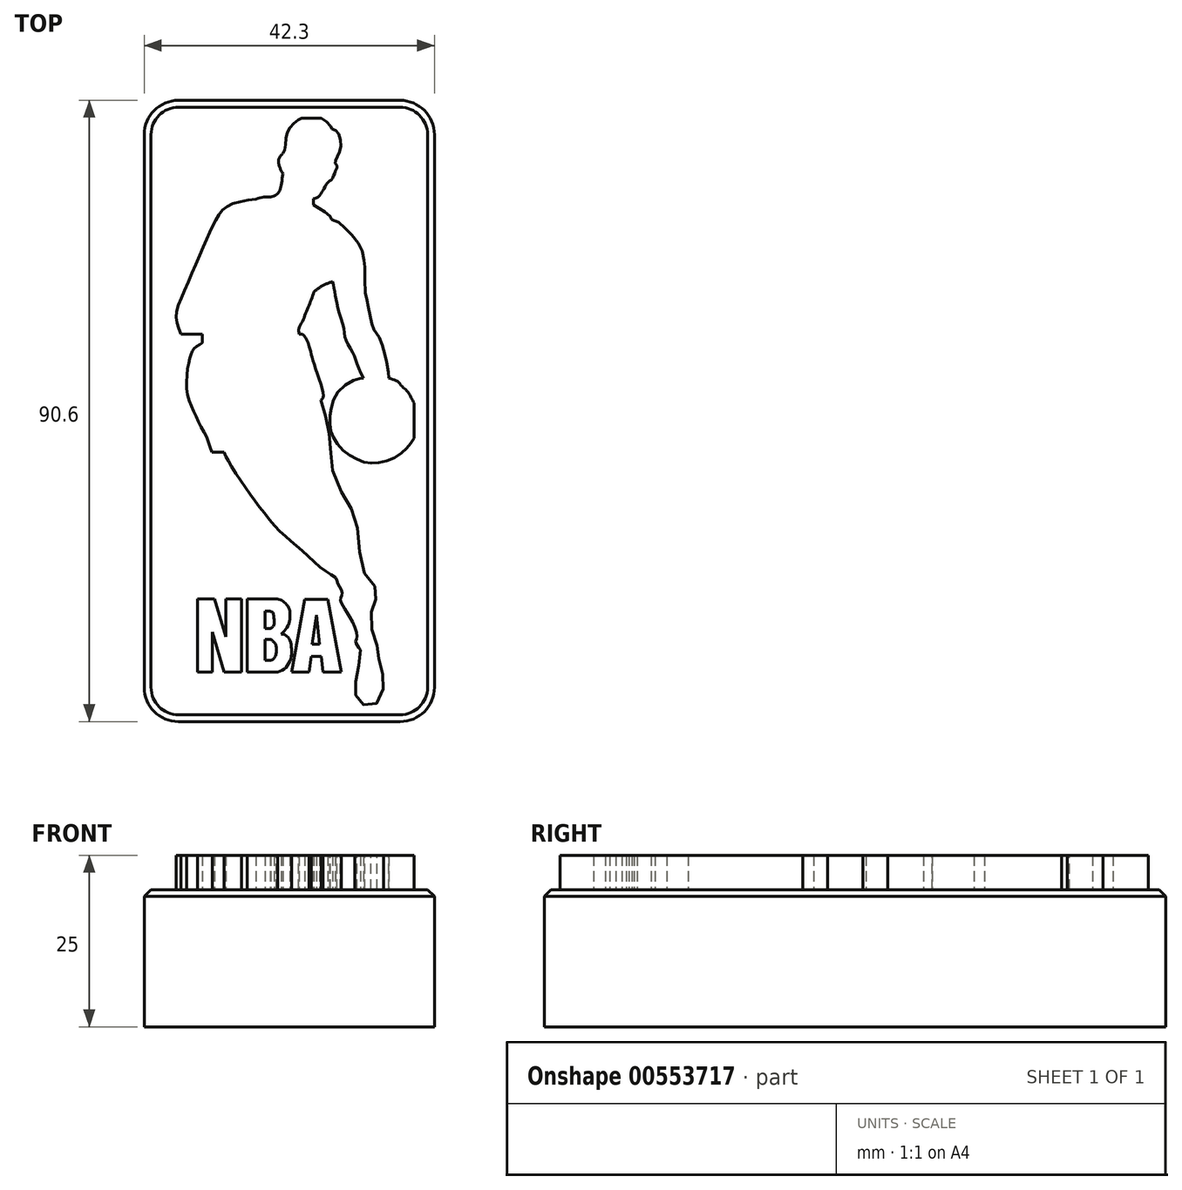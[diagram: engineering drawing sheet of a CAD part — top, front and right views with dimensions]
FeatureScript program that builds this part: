
annotation { "Feature Type Name" : "Feature", "Feature Type Description" : "" }
export const myFeature = defineFeature(function(context is Context, id is Id, definition is map)
    precondition{}
    {
        {
            var Q0;
            Q0=qCreatedBy(makeId("Top.planeOp"),FACE);
            var sketch = newSketch(context, id + "F0", { "sketchPlane" : qUnion([Q0])});
            skLineSegment(sketch, "E0", {"start": v(49.46, 96.34) * mm, "end": v(49.46, 0) * mm, "construction": true});
            skLineSegment(sketch, "E1", {"start": v(0, 48.17) * mm, "end": v(98.91, 48.17) * mm, "construction": true});
            skLineSegment(sketch, "E2.bottom", {"start": v(70.6, 93.47) * mm, "end": v(28.3, 93.47) * mm});
            skLineSegment(sketch, "E2.top", {"start": v(70.6, 2.87) * mm, "end": v(28.3, 2.87) * mm});
            skLineSegment(sketch, "E2.left", {"start": v(70.6, 93.47) * mm, "end": v(70.6, 2.87) * mm});
            skLineSegment(sketch, "E2.right", {"start": v(28.3, 93.47) * mm, "end": v(28.3, 2.87) * mm});
            skPoint(sketch, "E2.middle", {"position": v(49.46, 48.17) * mm});
            skSolve(sketch);
        }
        {
            var Q0;
            Q0 = qSketchRegion(id + "F0", true);
            extrude(context, id + "F1", {"entities" : qUnion([Q0]), "depth" : 20 * mm, "offsetDistance" : 25 * mm});
        }
        {
            var Q0;
            Q0=qCreatedBy(makeId("Top.planeOp"),FACE);
            var sketch = newSketch(context, id + "F2", { "sketchPlane" : qUnion([Q0])});
            skLineSegment(sketch, "E3", {"start": v(36.08, 10.07) * mm, "end": v(36.06, 20.74) * mm});
            skLineSegment(sketch, "E4", {"start": v(36.06, 20.74) * mm, "end": v(38.53, 20.74) * mm});
            skLineSegment(sketch, "E5", {"start": v(38.53, 20.74) * mm, "end": v(40.2, 15.23) * mm});
            skLineSegment(sketch, "E6", {"start": v(40.2, 15.23) * mm, "end": v(40.2, 20.74) * mm});
            skLineSegment(sketch, "E7", {"start": v(40.2, 20.74) * mm, "end": v(42.53, 20.74) * mm});
            skLineSegment(sketch, "E8", {"start": v(42.53, 20.74) * mm, "end": v(42.53, 10.07) * mm});
            skLineSegment(sketch, "E9", {"start": v(42.53, 10.07) * mm, "end": v(39.96, 10.07) * mm});
            skLineSegment(sketch, "E10", {"start": v(39.96, 10.07) * mm, "end": v(38.25, 15.94) * mm});
            skLineSegment(sketch, "E11", {"start": v(38.25, 15.94) * mm, "end": v(38.25, 10.07) * mm});
            skLineSegment(sketch, "E12", {"start": v(38.25, 10.07) * mm, "end": v(36.08, 10.07) * mm});
            skLineSegment(sketch, "E13", {"start": v(43.32, 10.07) * mm, "end": v(43.3, 20.74) * mm});
            skLineSegment(sketch, "E14", {"start": v(43.3, 20.74) * mm, "end": v(47.68, 20.74) * mm});
            skLineSegment(sketch, "E15", {"start": v(43.32, 10.07) * mm, "end": v(47.75, 10.08) * mm});
            skFitSpline(sketch, "E16", {"points": [v(47.75, 10.08) * mm, v(48.77, 10.58) * mm, v(49.49, 11.58) * mm, v(49.77, 12.75) * mm, v(49.75, 13.92) * mm, v(49.51, 14.83) * mm, v(49.15, 15.29) * mm, v(48.83, 15.52) * mm, v(48.28, 15.65) * mm], "startDerivative": vector(7.59, 2.72) * mm, "endDerivative": vector(-5.94, 1) * mm});
            skFitSpline(sketch, "E17", {"points": [v(48.28, 15.65) * mm, v(48.94, 16.33) * mm, v(49.47, 17.44) * mm, v(49.53, 18.32) * mm, v(49.49, 19.2) * mm, v(49.21, 19.77) * mm, v(48.72, 20.3) * mm, v(48.28, 20.6) * mm, v(47.68, 20.74) * mm], "startDerivative": vector(4.95, 4.43) * mm, "endDerivative": vector(-5.76, 0.93) * mm});
            skLineSegment(sketch, "E18", {"start": v(45.94, 19) * mm, "end": v(45.94, 16.5) * mm});
            skFitSpline(sketch, "E19", {"points": [v(45.94, 19) * mm, v(46.53, 19) * mm, v(47, 18.82) * mm, v(47.2, 18.33) * mm, v(47.25, 17.67) * mm, v(47.25, 17.06) * mm, v(46.99, 16.64) * mm, v(46.7, 16.44) * mm], "startDerivative": vector(3.88, 0.21) * mm, "endDerivative": vector(-2.46, -1.47) * mm});
            skLineSegment(sketch, "E20", {"start": v(46.7, 16.44) * mm, "end": v(45.94, 16.44) * mm});
            skLineSegment(sketch, "E21", {"start": v(45.94, 16.44) * mm, "end": v(45.94, 16.5) * mm});
            skLineSegment(sketch, "E22", {"start": v(45.94, 14.83) * mm, "end": v(45.94, 11.81) * mm});
            skLineSegment(sketch, "E23", {"start": v(45.94, 11.81) * mm, "end": v(46.79, 11.81) * mm});
            skFitSpline(sketch, "E24", {"points": [v(46.79, 11.81) * mm, v(47.22, 12.07) * mm, v(47.53, 12.8) * mm, v(47.56, 13.65) * mm, v(47.4, 14.25) * mm, v(47, 14.66) * mm, v(46.79, 14.84) * mm], "startDerivative": vector(3, 1.25) * mm, "endDerivative": vector(-1.62, 1.47) * mm});
            skLineSegment(sketch, "E25", {"start": v(45.94, 14.83) * mm, "end": v(46.79, 14.84) * mm});
            skLineSegment(sketch, "E26", {"start": v(49.8, 10.08) * mm, "end": v(50.27, 10.08) * mm});
            skLineSegment(sketch, "E27", {"start": v(50.27, 10.08) * mm, "end": v(52.35, 10.09) * mm});
            skLineSegment(sketch, "E28", {"start": v(52.35, 10.09) * mm, "end": v(52.64, 12.4) * mm});
            skLineSegment(sketch, "E29", {"start": v(52.64, 12.4) * mm, "end": v(54.13, 12.4) * mm});
            skLineSegment(sketch, "E30", {"start": v(54.13, 12.4) * mm, "end": v(54.35, 10.08) * mm});
            skLineSegment(sketch, "E31", {"start": v(54.35, 10.08) * mm, "end": v(57.02, 10.1) * mm});
            skLineSegment(sketch, "E32", {"start": v(57.02, 10.1) * mm, "end": v(55.07, 20.7) * mm});
            skLineSegment(sketch, "E33", {"start": v(55.07, 20.7) * mm, "end": v(51.71, 20.7) * mm});
            skLineSegment(sketch, "E34", {"start": v(51.71, 20.7) * mm, "end": v(49.8, 10.08) * mm});
            skLineSegment(sketch, "E35", {"start": v(52.8, 14.19) * mm, "end": v(53.85, 14.19) * mm});
            skLineSegment(sketch, "E36", {"start": v(53.85, 14.19) * mm, "end": v(53.45, 18.42) * mm});
            skLineSegment(sketch, "E37", {"start": v(53.45, 18.42) * mm, "end": v(52.8, 14.19) * mm});
            skSolve(sketch);
        }
        {
            var Q0;
            Q0 = qSketchRegion(id + "F2", true);
            extrude(context, id + "F3", {"entities" : qUnion([Q0]), "operationType" : NewBodyOperationType.ADD, "depth" : 25 * mm, "offsetDistance" : 25 * mm});
        }
        {
            var Q0;
            Q0=qCreatedBy(makeId("Top.planeOp"),FACE);
            var sketch = newSketch(context, id + "F4", { "sketchPlane" : qUnion([Q0])});
            skFitSpline(sketch, "E38", {"points": [v(56.13, 84.27) * mm, v(56.38, 84.06) * mm, v(56.32, 83.43) * mm, v(56.07, 82.86) * mm, v(55.63, 81.93) * mm, v(55.23, 81.64) * mm, v(55.06, 81.53) * mm, v(54.6, 80.79) * mm, v(54.22, 80.1) * mm, v(53.88, 79.58) * mm, v(53.44, 79.24) * mm, v(52.94, 79.1) * mm], "startDerivative": vector(4.5, -2.2) * mm, "endDerivative": vector(-5.95, -1.06) * mm});
            skFitSpline(sketch, "E39", {"points": [v(52.94, 79.1) * mm, v(52.94, 78.25) * mm], "startDerivative": vector(0, -0.86) * mm, "endDerivative": vector(0, -0.86) * mm});
            skFitSpline(sketch, "E40", {"points": [v(52.94, 78.25) * mm, v(55.23, 76.82) * mm, v(55.42, 76.5) * mm, v(55.44, 76.18) * mm, v(56.1, 75.95) * mm, v(57.05, 75.4) * mm, v(58.11, 74.32) * mm, v(59.44, 72.75) * mm, v(60.08, 71.4) * mm, v(60.4, 69.88) * mm, v(60.48, 68.98) * mm, v(60.5, 65.62) * mm, v(60.72, 64.46) * mm, v(60.95, 63.55) * mm, v(61.19, 62.38) * mm, v(61.46, 61.03) * mm, v(61.64, 60.25) * mm, v(62.44, 59.13) * mm, v(63.02, 57.81) * mm, v(63.42, 56.2) * mm, v(63.72, 55.04) * mm, v(63.95, 53.3) * mm, v(63.93, 52.94) * mm], "startDerivative": vector(43.04, -24.8) * mm, "endDerivative": vector(-1.36, -11.13) * mm});
            skFitSpline(sketch, "E41", {"points": [v(63.93, 52.94) * mm, v(65.3, 52.44) * mm, v(65.82, 51.82) * mm, v(66.57, 51.15) * mm, v(67.18, 50.18) * mm, v(67.65, 49.33) * mm], "startDerivative": vector(6.8, -1.68) * mm, "endDerivative": vector(2.4, -4.31) * mm});
            skFitSpline(sketch, "E42", {"points": [v(67.65, 49.33) * mm, v(67.65, 44.18) * mm], "startDerivative": vector(0, -5.16) * mm, "endDerivative": vector(0, -5.16) * mm});
            skFitSpline(sketch, "E43", {"points": [v(67.65, 44.18) * mm, v(66.97, 43.24) * mm, v(66.13, 42.32) * mm, v(64.47, 41.17) * mm, v(62.47, 40.6) * mm, v(60.8, 40.62) * mm, v(59.17, 41.23) * mm, v(57.4, 42.34) * mm, v(56.09, 43.95) * mm, v(55.52, 45.24) * mm, v(55.39, 47.05) * mm, v(55.66, 48.91) * mm, v(56.6, 51.04) * mm, v(58.92, 52.66) * mm, v(59.94, 52.94) * mm, v(60.26, 52.94) * mm], "startDerivative": vector(-11.97, -17.16) * mm, "endDerivative": vector(9.83, -0.58) * mm});
            skFitSpline(sketch, "E44", {"points": [v(60.26, 52.94) * mm, v(59.23, 55.35) * mm, v(58.66, 56.77) * mm, v(57.7, 58.56) * mm, v(57.43, 59.99) * mm, v(56.7, 62.7) * mm, v(56.23, 64.65) * mm, v(55.98, 66) * mm, v(55.78, 67.05) * mm], "startDerivative": vector(-7.83, 17.22) * mm, "endDerivative": vector(-2.09, 10.68) * mm});
            skFitSpline(sketch, "E45", {"points": [v(55.78, 67.05) * mm, v(54.3, 66.44) * mm, v(53.03, 65.52) * mm], "startDerivative": vector(-3.05, -1.05) * mm, "endDerivative": vector(-2.45, -2) * mm});
            skFitSpline(sketch, "E46", {"points": [v(53.03, 65.52) * mm, v(52.58, 64.2) * mm, v(51.95, 62.72) * mm, v(51.36, 61.21) * mm, v(50.82, 60.12) * mm, v(50.91, 59.4) * mm], "startDerivative": vector(-1.92, -6.3) * mm, "endDerivative": vector(1.44, -4.65) * mm});
            skFitSpline(sketch, "E47", {"points": [v(50.91, 59.4) * mm, v(51.55, 59.24) * mm, v(52.44, 57.38) * mm, v(53.03, 55.16) * mm, v(54.43, 50.33) * mm, v(54.05, 49.77) * mm], "startDerivative": vector(5.44, 0.14) * mm, "endDerivative": vector(-4.4, -2.9) * mm});
            skFitSpline(sketch, "E48", {"points": [v(54.05, 49.77) * mm, v(54.73, 47.48) * mm, v(55.23, 45.12) * mm, v(55.52, 41.97) * mm, v(55.78, 39.46) * mm, v(57.5, 35.56) * mm, v(58.9, 33.04) * mm, v(59.62, 29) * mm, v(60.26, 24.8) * mm, v(61.78, 22.84) * mm, v(62.25, 21.32) * mm, v(61.75, 19.99) * mm, v(61.41, 18.58) * mm, v(61.55, 15.9) * mm, v(62.25, 13.82) * mm, v(62.39, 12.62) * mm, v(62.93, 10.42) * mm, v(63.18, 8.86) * mm, v(62.96, 6.61) * mm, v(61.78, 5.28) * mm, v(60.26, 5.35) * mm, v(59.38, 6.27) * mm, v(59.04, 7.27) * mm, v(59.24, 9.2) * mm, v(59.62, 11.3) * mm, v(59.8, 13.32) * mm], "startDerivative": vector(17.19, -55.33) * mm, "endDerivative": vector(3.4, 52.46) * mm});
            skFitSpline(sketch, "E49", {"points": [v(59.8, 13.32) * mm, v(59.38, 13.98) * mm, v(59.13, 14.61) * mm, v(59.35, 15.3) * mm, v(58.15, 18.35) * mm, v(57.15, 19.96) * mm, v(56.93, 20.92) * mm, v(57.18, 21.57) * mm, v(56.68, 22.77) * mm, v(56.25, 23.86) * mm], "startDerivative": vector(-4.75, 7.09) * mm, "endDerivative": vector(-3.14, 9.49) * mm});
            skFitSpline(sketch, "E50", {"points": [v(56.25, 23.86) * mm, v(54.05, 25.32) * mm, v(50.91, 28.18) * mm, v(48.25, 30.48) * mm, v(45.53, 33.66) * mm, v(43.03, 37.06) * mm, v(40.69, 40.68) * mm, v(39.95, 42.15) * mm], "startDerivative": vector(-17, 10) * mm, "endDerivative": vector(-6.02, 13.27) * mm});
            skFitSpline(sketch, "E51", {"points": [v(39.95, 42.15) * mm, v(38.15, 42.15) * mm], "startDerivative": vector(-1.8, 0) * mm, "endDerivative": vector(-1.8, 0) * mm});
            skFitSpline(sketch, "E52", {"points": [v(38.15, 42.15) * mm, v(37.48, 44.18) * mm, v(36.33, 46.41) * mm, v(35.3, 48.66) * mm, v(34.52, 51.21) * mm, v(34.68, 54.49) * mm, v(35.06, 56.2) * mm, v(35.44, 57.08) * mm, v(36.09, 57.7) * mm, v(36.8, 58.11) * mm], "startDerivative": vector(-4.74, 16.89) * mm, "endDerivative": vector(9.78, 5.16) * mm});
            skFitSpline(sketch, "E53", {"points": [v(36.8, 58.11) * mm, v(36.8, 59.4) * mm], "startDerivative": vector(0, 1.3) * mm, "endDerivative": vector(0, 1.3) * mm});
            skFitSpline(sketch, "E54", {"points": [v(36.8, 59.4) * mm, v(33.68, 59.4) * mm], "startDerivative": vector(-3.13, 0) * mm, "endDerivative": vector(-3.13, 0) * mm});
            skFitSpline(sketch, "E55", {"points": [v(33.68, 59.4) * mm, v(32.96, 61.88) * mm, v(34.1, 65.52) * mm, v(36.8, 71.87) * mm, v(38.68, 75.91) * mm, v(40.4, 78) * mm, v(44.62, 79.07) * mm], "startDerivative": vector(-8.1, 18.08) * mm, "endDerivative": vector(27.69, 3.84) * mm});
            skFitSpline(sketch, "E56", {"points": [v(44.62, 79.07) * mm, v(45.92, 79.38) * mm, v(46.95, 79.42) * mm, v(47.86, 79.95) * mm, v(48.24, 80.94) * mm, v(48.51, 82.77) * mm], "startDerivative": vector(6.45, 2) * mm, "endDerivative": vector(1.03, 8.03) * mm});
            skFitSpline(sketch, "E57", {"points": [v(48.51, 82.77) * mm, v(48.02, 83.84) * mm, v(47.94, 84.94) * mm, v(48.51, 85.74) * mm], "startDerivative": vector(-1.61, 2.97) * mm, "endDerivative": vector(2.25, 2.32) * mm});
            skFitSpline(sketch, "E58", {"points": [v(48.51, 85.74) * mm, v(48.85, 86.5) * mm, v(49.05, 88.41) * mm, v(49.7, 89.67) * mm, v(50.91, 90.7) * mm, v(51.52, 90.9) * mm, v(53.31, 90.85) * mm, v(54.05, 90.9) * mm, v(55.33, 89.86) * mm, v(55.78, 89.25) * mm, v(56.36, 88.98) * mm, v(56.97, 87.38) * mm, v(56.7, 85.74) * mm, v(56.23, 84.8) * mm, v(56.13, 84.27) * mm], "startDerivative": vector(6.68, 10.5) * mm, "endDerivative": vector(-0.94, -10.26) * mm});
            skSolve(sketch);
        }
        {
            var Q0;
            Q0 = qSketchRegion(id + "F4", true);
            extrude(context, id + "F5", {"entities" : qUnion([Q0]), "operationType" : NewBodyOperationType.ADD, "depth" : 25 * mm, "offsetDistance" : 25 * mm});
        }
        {
            var Q0;
            Q0=makeQuery(id+"F1.opExtrude","SWEPT_EDGE",EDGE,{"disambiguationData":[OSD([sQuery(id+"F0.wireOp",EDGE,"E2.bottom"),sQuery(id+"F0.wireOp",EDGE,"E2.right")])]});
            var Q1;
            Q1=makeQuery(id+"F1.opExtrude","SWEPT_EDGE",EDGE,{"disambiguationData":[OSD([sQuery(id+"F0.wireOp",EDGE,"E2.bottom"),sQuery(id+"F0.wireOp",EDGE,"E2.left")])]});
            var Q2;
            Q2=makeQuery(id+"F1.opExtrude","SWEPT_EDGE",EDGE,{"disambiguationData":[OSD([sQuery(id+"F0.wireOp",EDGE,"E2.top"),sQuery(id+"F0.wireOp",EDGE,"E2.right")])]});
            var Q3;
            Q3=makeQuery(id+"F1.opExtrude","SWEPT_EDGE",EDGE,{"disambiguationData":[OSD([sQuery(id+"F0.wireOp",EDGE,"E2.top"),sQuery(id+"F0.wireOp",EDGE,"E2.left")])]});
            fillet(context, id + "F6", {"entities" : qUnion([Q0, Q1, Q2, Q3]), "radius" : 5 * mm, "tangentPropagation" : true, "allowEdgeOverflow" : false});
        }
        {
            var Q0;
            Q0=makeQuery(id+"F1.opExtrude","CAP_EDGE",EDGE,{"disambiguationData":[OSD([sQuery(id+"F0.wireOp",EDGE,"E2.right")])],"isStart":false});
            chamfer(context, id + "F7", {"entities" : qUnion([Q0]), "width" : 1 * mm, "tangentPropagation" : true});
        }
    });
